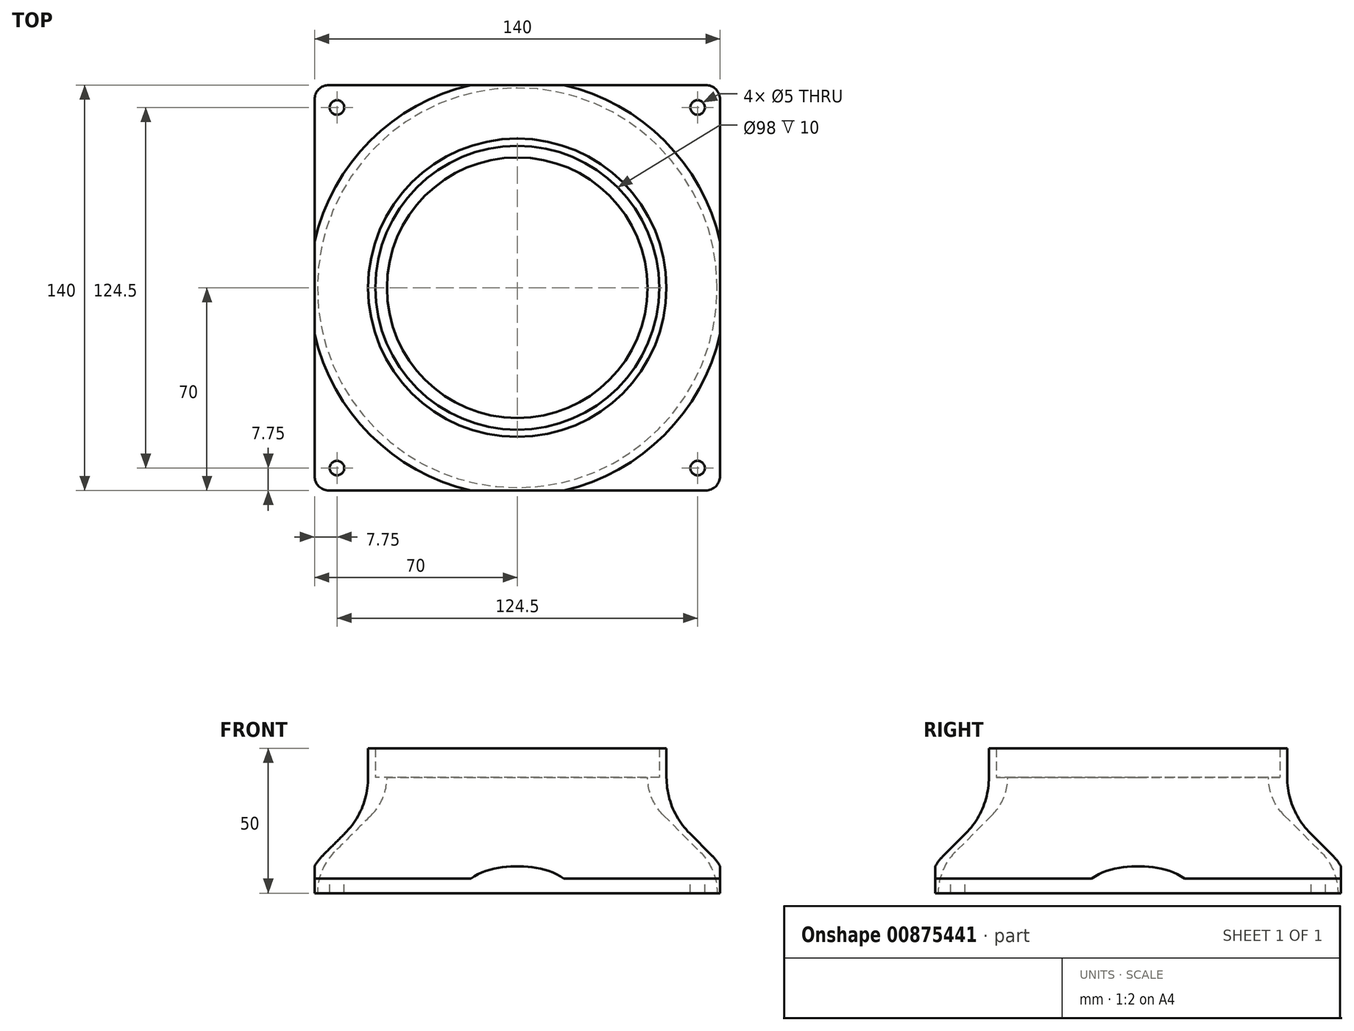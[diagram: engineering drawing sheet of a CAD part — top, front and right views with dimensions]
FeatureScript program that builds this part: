
annotation { "Feature Type Name" : "Feature", "Feature Type Description" : "" }
export const myFeature = defineFeature(function(context is Context, id is Id, definition is map)
    precondition{}
    {
        {
            var Q0;
            Q0=qCreatedBy(makeId("Top.planeOp"),FACE);
            var sketch = newSketch(context, id + "F0", { "sketchPlane" : qUnion([Q0])});
            skCircle(sketch, "E0", {"center": v(0, 0) * mm, "radius": 69 * mm});
            skCircle(sketch, "E1", {"center": v(0, 0) * mm, "radius": 72.5 * mm});
            skSolve(sketch);
        }
        {
            var Q0;
            Q0=qCreatedBy(makeId("Top.planeOp"),FACE);
            cPlane(context, id + "F1", {"entities" : qUnion([Q0]), "cplaneType" : CPlaneType.OFFSET, "offset" : 40 * mm, "width" : 150 * mm, "height" : 150 * mm});
        }
        {
            var Q0;
            Q0=qCreatedBy(id+"F1.planeOp",FACE);
            var sketch = newSketch(context, id + "F2", { "sketchPlane" : qUnion([Q0])});
            skCircle(sketch, "E2", {"center": v(0, 0) * mm, "radius": 45 * mm});
            skCircle(sketch, "E3", {"center": v(0, 0) * mm, "radius": 51.5 * mm});
            skCircle(sketch, "E4", {"center": v(0, 0) * mm, "radius": 49 * mm});
            skSolve(sketch);
        }
        {
            var Q0;
            Q0=qCreatedBy(makeId("Front.planeOp"),FACE);
            var sketch = newSketch(context, id + "F3", { "sketchPlane" : qUnion([Q0])});
            skLineSegment(sketch, "E5", {"start": v(69, 0) * mm, "end": v(72.5, 0) * mm});
            skLineSegment(sketch, "E6", {"start": v(51.5, 40) * mm, "end": v(45, 40) * mm});
            skLineSegment(sketch, "E7", {"start": v(0, 0) * mm, "end": v(0, 40) * mm, "construction": true});
            skArc(sketch, "E8", {"start": v(45, 40) * mm, "mid": v(46.4, 32.92) * mm, "end": v(50.42, 26.92) * mm});
            skLineSegment(sketch, "E9", {"start": v(50.42, 26.92) * mm, "end": v(63.1, 14.23) * mm});
            skLineSegment(sketch, "E10", {"start": v(59.52, 20.65) * mm, "end": v(67.08, 13.08) * mm});
            skArc(sketch, "E11", {"start": v(69, 0) * mm, "mid": v(67.47, 7.7) * mm, "end": v(63.1, 14.23) * mm});
            skArc(sketch, "E12", {"start": v(72.5, 0) * mm, "mid": v(71.1, 7.08) * mm, "end": v(67.08, 13.08) * mm});
            skLineSegment(sketch, "E13", {"start": v(72.5, 0) * mm, "end": v(72.5, 22.83) * mm, "construction": true});
            skLineSegment(sketch, "E14", {"start": v(45, 40) * mm, "end": v(45, 26.6) * mm, "construction": true});
            skArc(sketch, "E15", {"start": v(51.5, 40) * mm, "mid": v(53.58, 29.53) * mm, "end": v(59.52, 20.65) * mm});
            skLineSegment(sketch, "E16", {"start": v(51.5, 40) * mm, "end": v(51.5, 22.8) * mm, "construction": true});
            skLineSegment(sketch, "E17", {"start": v(69, 0) * mm, "end": v(69, 23.09) * mm, "construction": true});
            skSolve(sketch);
        }
        {
            var Q0;
            Q0=makeQuery(id+"F3.imprint","IMPRINT",FACE,{"disambiguationData":[TD([[makeQuery(id+"F3.imprint","IMPRINT",EDGE,{"derivedFrom":sQuery(id+"F3.wireOp",EDGE,"E5")}),1.0]])]});
            var Q1;
            Q1=sQuery(id+"F3.wireOp",EDGE,"E7");
            revolve(context, id + "F4", {"entities" : qUnion([Q0]), "axis" : qUnion([Q1]), "revolveType" : RevolveType.FULL});
        }
        {
            var Q0;
            Q0=qSketchRegion(id+"F2",true);
            extrude(context, id + "F5", {"entities" : qUnion([Q0]), "operationType" : NewBodyOperationType.ADD, "offsetDistance" : 25 * mm, "depth" : 10 * mm});
        }
        {
            var Q0;
            Q0=qCreatedBy(makeId("Top.planeOp"),FACE);
            cPlane(context, id + "F6", {"entities" : qUnion([Q0]), "cplaneType" : CPlaneType.OFFSET, "offset" : 5 * mm, "width" : 150 * mm, "height" : 150 * mm});
        }
        {
            var Q0;
            Q0=qCreatedBy(id+"F6.planeOp",FACE);
            var sketch = newSketch(context, id + "F7", { "sketchPlane" : qUnion([Q0])});
            skLineSegment(sketch, "E18.bottom", {"start": v(-62.25, 62.25) * mm, "end": v(62.25, 62.25) * mm, "construction": true});
            skLineSegment(sketch, "E18.top", {"start": v(-62.25, -62.25) * mm, "end": v(62.25, -62.25) * mm, "construction": true});
            skLineSegment(sketch, "E18.left", {"start": v(-62.25, 62.25) * mm, "end": v(-62.25, -62.25) * mm, "construction": true});
            skLineSegment(sketch, "E18.right", {"start": v(62.25, 62.25) * mm, "end": v(62.25, -62.25) * mm, "construction": true});
            skPoint(sketch, "E18.middle", {"position": v(0, 0) * mm});
            skCircle(sketch, "E19", {"center": v(-62.25, 62.25) * mm, "radius": 2.5 * mm});
            skCircle(sketch, "E20", {"center": v(-62.25, -62.25) * mm, "radius": 2.5 * mm});
            skCircle(sketch, "E21", {"center": v(62.25, -62.25) * mm, "radius": 2.5 * mm});
            skCircle(sketch, "E22", {"center": v(62.25, 62.25) * mm, "radius": 2.5 * mm});
            skArc(sketch, "E23", {"start": v(-70, -16.03) * mm, "mid": v(-50.78, -50.78) * mm, "end": v(-16.03, -70) * mm});
            skLineSegment(sketch, "E24.bottom", {"start": v(-65, 70) * mm, "end": v(65, 70) * mm});
            skLineSegment(sketch, "E24.top", {"start": v(-65, -70) * mm, "end": v(65, -70) * mm});
            skLineSegment(sketch, "E24.left", {"start": v(-70, 65) * mm, "end": v(-70, -65) * mm});
            skLineSegment(sketch, "E24.right", {"start": v(70, 65) * mm, "end": v(70, -65) * mm});
            skPoint(sketch, "E25.visualSharp", {"position": v(70, 70) * mm});
            skArc(sketch, "E25.filletArc", {"start": v(70, 65) * mm, "mid": v(68.54, 68.54) * mm, "end": v(65, 70) * mm});
            skPoint(sketch, "E26.visualSharp", {"position": v(-70, 70) * mm});
            skArc(sketch, "E26.filletArc", {"start": v(-65, 70) * mm, "mid": v(-68.54, 68.54) * mm, "end": v(-70, 65) * mm});
            skPoint(sketch, "E27.visualSharp", {"position": v(-70, -70) * mm});
            skArc(sketch, "E27.filletArc", {"start": v(-70, -65) * mm, "mid": v(-68.54, -68.54) * mm, "end": v(-65, -70) * mm});
            skPoint(sketch, "E28.visualSharp", {"position": v(70, -70) * mm});
            skArc(sketch, "E28.filletArc", {"start": v(65, -70) * mm, "mid": v(68.54, -68.54) * mm, "end": v(70, -65) * mm});
            skArc(sketch, "E29.trimOffspring", {"start": v(16.03, -70) * mm, "mid": v(50.78, -50.78) * mm, "end": v(70, -16.03) * mm});
            skArc(sketch, "E30.trimOffspring", {"start": v(70, 16.03) * mm, "mid": v(50.78, 50.78) * mm, "end": v(16.03, 70) * mm});
            skArc(sketch, "E31.trimOffspring", {"start": v(-16.03, 70) * mm, "mid": v(-50.78, 50.78) * mm, "end": v(-70, 16.03) * mm});
            skPoint(sketch, "E32.MirrorCS.end.orphan", {"position": v(-67.25, -25.19) * mm});
            skPoint(sketch, "E33.MirrorCS.end.orphan", {"position": v(-25.19, -67.25) * mm});
            skPoint(sketch, "E34.MirrorCS.end.orphan", {"position": v(-67.25, 25.19) * mm});
            skPoint(sketch, "E35.MirrorCS.end.orphan", {"position": v(-25.19, 67.25) * mm});
            skPoint(sketch, "E36.MirrorCS.end.orphan", {"position": v(67.25, 25.19) * mm});
            skPoint(sketch, "E37.MirrorCS.end.orphan", {"position": v(25.19, 67.25) * mm});
            skPoint(sketch, "E38.end.orphan", {"position": v(25.19, -67.25) * mm});
            skPoint(sketch, "E39.end.orphan", {"position": v(67.25, -25.19) * mm});
            skSolve(sketch);
        }
        {
            var Q0;
            Q0=makeQuery(id+"F7.imprint","IMPRINT",FACE,{"disambiguationData":[TD([[makeQuery(id+"F7.imprint","IMPRINT",EDGE,{"derivedFrom":sQuery(id+"F7.wireOp",EDGE,"E19")}),-1.0]])]});
            var Q1;
            Q1=makeQuery(id+"F7.imprint","IMPRINT",FACE,{"disambiguationData":[TD([[makeQuery(id+"F7.imprint","IMPRINT",EDGE,{"derivedFrom":sQuery(id+"F7.wireOp",EDGE,"E20")}),-1.0]])]});
            var Q2;
            Q2=makeQuery(id+"F7.imprint","IMPRINT",FACE,{"disambiguationData":[TD([[makeQuery(id+"F7.imprint","IMPRINT",EDGE,{"derivedFrom":sQuery(id+"F7.wireOp",EDGE,"E21")}),-1.0]])]});
            var Q3;
            Q3=makeQuery(id+"F7.imprint","IMPRINT",FACE,{"disambiguationData":[TD([[makeQuery(id+"F7.imprint","IMPRINT",EDGE,{"derivedFrom":sQuery(id+"F7.wireOp",EDGE,"E22")}),-1.0]])]});
            extrude(context, id + "F8", {"entities" : qUnion([Q0, Q1, Q2, Q3]), "operationType" : NewBodyOperationType.ADD, "oppositeDirection" : true, "depth" : 5 * mm});
        }
        {
            var Q0;
            Q0=qCreatedBy(makeId("Top.planeOp"),FACE);
            var sketch = newSketch(context, id + "F9", { "sketchPlane" : qUnion([Q0])});
            skLineSegment(sketch, "E40.bottom", {"start": v(-70, -70) * mm, "end": v(70, -70) * mm});
            skLineSegment(sketch, "E40.top", {"start": v(-70, 70) * mm, "end": v(70, 70) * mm});
            skLineSegment(sketch, "E40.left", {"start": v(-70, -70) * mm, "end": v(-70, 70) * mm});
            skLineSegment(sketch, "E40.right", {"start": v(70, -70) * mm, "end": v(70, 70) * mm});
            skPoint(sketch, "E40.middle", {"position": v(0, 0) * mm});
            skLineSegment(sketch, "E41.bottom", {"start": v(80.46, -81.55) * mm, "end": v(-80.46, -81.55) * mm});
            skLineSegment(sketch, "E41.top", {"start": v(80.46, 81.55) * mm, "end": v(-80.46, 81.55) * mm});
            skLineSegment(sketch, "E41.left", {"start": v(80.46, -81.55) * mm, "end": v(80.46, 81.55) * mm});
            skLineSegment(sketch, "E41.right", {"start": v(-80.46, -81.55) * mm, "end": v(-80.46, 81.55) * mm});
            skSolve(sketch);
        }
        {
            var Q0;
            Q0=qSketchRegion(id+"F9",true);
            var Q1;
            Q1=makeQuery(id+"F8.opExtrude","CAP_FACE",FACE,{"disambiguationData":[OSD([sQuery(id+"F7.wireOp",EDGE,"E20"),sQuery(id+"F7.wireOp",EDGE,"E23"),sQuery(id+"F7.wireOp",EDGE,"E24.top"),sQuery(id+"F7.wireOp",EDGE,"E24.left"),sQuery(id+"F7.wireOp",EDGE,"E27.filletArc")])],"isStart":true});
            extrude(context, id + "F10", {"entities" : qUnion([Q0]), "operationType" : NewBodyOperationType.REMOVE, "depth" : 10 * mm, "endBoundEntityFace" : qUnion([Q1]), "offsetDistance" : 25 * mm});
        }
    });
